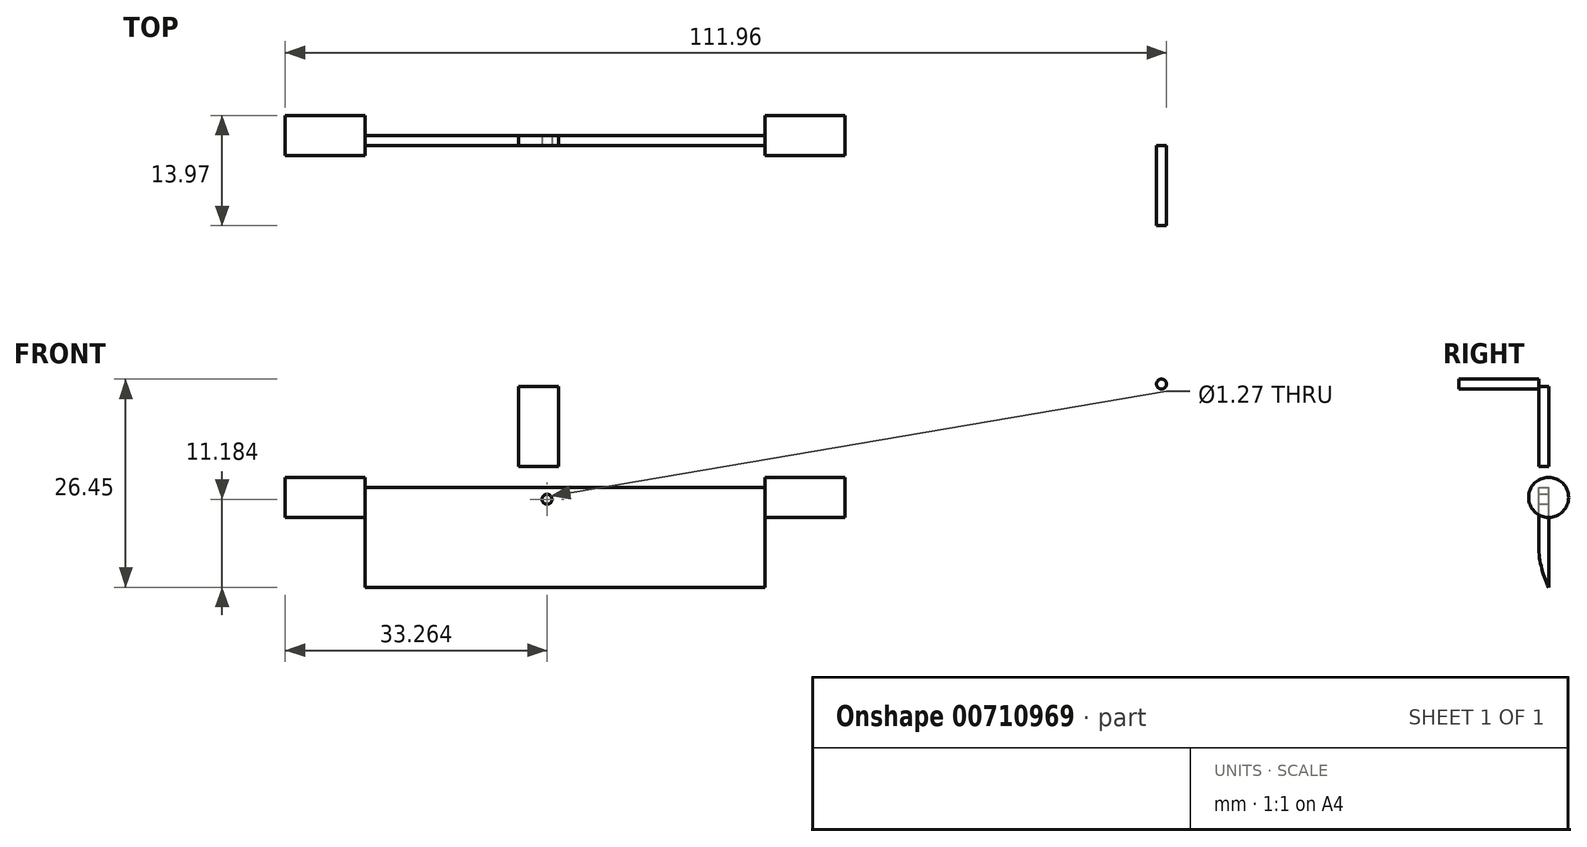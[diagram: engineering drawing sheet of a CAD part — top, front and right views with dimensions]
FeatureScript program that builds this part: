
annotation { "Feature Type Name" : "Feature", "Feature Type Description" : "" }
export const myFeature = defineFeature(function(context is Context, id is Id, definition is map)
    precondition{}
    {
        {
            var Q0;
            Q0=qCreatedBy(makeId("Front.planeOp"),FACE);
            var sketch = newSketch(context, id + "F0", { "sketchPlane" : qUnion([Q0])});
            skLineSegment(sketch, "E0.bottom", {"start": v(2.2, 26.26) * mm, "end": v(-48.6, 26.26) * mm});
            skLineSegment(sketch, "E0.top", {"start": v(2.2, 38.96) * mm, "end": v(-48.6, 38.96) * mm});
            skLineSegment(sketch, "E0.left", {"start": v(2.2, 26.26) * mm, "end": v(2.2, 38.96) * mm});
            skLineSegment(sketch, "E0.right", {"start": v(-48.6, 26.26) * mm, "end": v(-48.6, 38.96) * mm});
            skPoint(sketch, "E0.middle", {"position": v(-23.2, 32.6) * mm});
            skLineSegment(sketch, "E1", {"start": v(-48.6, 37.69) * mm, "end": v(-58.75, 37.69) * mm});
            skLineSegment(sketch, "E2", {"start": v(-58.75, 37.69) * mm, "end": v(-58.75, 35.15) * mm});
            skLineSegment(sketch, "E3", {"start": v(-58.75, 35.15) * mm, "end": v(-48.6, 35.15) * mm});
            skLineSegment(sketch, "E4", {"start": v(2.2, 37.69) * mm, "end": v(12.37, 37.69) * mm});
            skLineSegment(sketch, "E5", {"start": v(12.37, 37.69) * mm, "end": v(12.37, 35.15) * mm});
            skLineSegment(sketch, "E6", {"start": v(12.37, 35.15) * mm, "end": v(2.2, 35.15) * mm});
            skLineSegment(sketch, "E7", {"start": v(-29.08, 45.04) * mm, "end": v(-29.08, 41.6) * mm});
            skLineSegment(sketch, "E8", {"start": v(-29.08, 41.6) * mm, "end": v(-24, 41.6) * mm});
            skLineSegment(sketch, "E9", {"start": v(-24, 41.6) * mm, "end": v(-24, 51.75) * mm});
            skLineSegment(sketch, "E10", {"start": v(-24, 51.75) * mm, "end": v(-29.08, 51.75) * mm});
            skLineSegment(sketch, "E11", {"start": v(-29.08, 51.75) * mm, "end": v(-29.08, 45.04) * mm});
            skSolve(sketch);
        }
        {
            var Q0;
            {var subQ0=sQuery(id+"F0.wireOp",EDGE,"E1");Q0=makeQuery(id+"F0.imprint","IMPRINT",FACE,{"disambiguationData":[TD([[makeQuery(id+"F0.imprint","IMPRINT",EDGE,{"derivedFrom":subQ0}),1.0]])]});}
            var Q1;
            Q1=sQuery(id+"F0.wireOp",EDGE,"E1");
            revolve(context, id + "F1", {"surfaceOperationType" : NewSurfaceOperationType.NEW, "entities" : qUnion([Q0]), "axis" : qUnion([Q1]), "revolveType" : RevolveType.FULL});
        }
        {
            var Q0;
            {var subQ0=sQuery(id+"F0.wireOp",EDGE,"E4");Q0=makeQuery(id+"F0.imprint","IMPRINT",FACE,{"disambiguationData":[TD([[makeQuery(id+"F0.imprint","IMPRINT",EDGE,{"derivedFrom":subQ0}),-1.0]])]});}
            var Q1;
            Q1=sQuery(id+"F0.wireOp",EDGE,"E4");
            revolve(context, id + "F2", {"surfaceOperationType" : NewSurfaceOperationType.NEW, "entities" : qUnion([Q0]), "axis" : qUnion([Q1]), "revolveType" : RevolveType.FULL});
        }
        {
            var Q0;
            {var subQ3=sQuery(id+"F0.wireOp",EDGE,"E0.bottom");Q0=makeQuery(id+"F0.imprint","IMPRINT",FACE,{"disambiguationData":[TD([[makeQuery(id+"F0.imprint","IMPRINT",EDGE,{"derivedFrom":subQ3}),-1.0]])]});}
            extrude(context, id + "F3", {"entities" : qUnion([Q0]), "depth" : 1.27 * mm, "offsetDistance" : 25.4 * mm});
        }
        {
            var Q0;
            Q0=makeQuery(id+"F3.opExtrude","CAP_EDGE",EDGE,{"disambiguationData":[OSD([sQuery(id+"F0.wireOp",EDGE,"E0.bottom")])],"isStart":false});
            fillet(context, id + "F4", {"entities" : qUnion([Q0]), "radius" : 12.7 * mm, "tangentPropagation" : true, "rho" : 0.5, "crossSection" : FilletCrossSection.CONIC, "allowEdgeOverflow" : false});
        }
        {
            var Q0;
            Q0=makeQuery(id+"F3.opExtrude","CAP_FACE",FACE,{"disambiguationData":[OSD([sQuery(id+"F0.wireOp",EDGE,"E0.bottom"),sQuery(id+"F0.wireOp",EDGE,"E0.top"),sQuery(id+"F0.wireOp",EDGE,"E0.left"),sQuery(id+"F0.wireOp",EDGE,"E0.right")])],"isStart":false});
            var sketch = newSketch(context, id + "F5", { "sketchPlane" : qUnion([Q0])});
            skCircle(sketch, "E12", {"center": v(-25.49, 37.44) * mm, "radius": 0.64 * mm});
            skCircle(sketch, "E13", {"center": v(52.57, 52.08) * mm, "radius": 0.64 * mm});
            skSolve(sketch);
        }
        {
            var Q0;
            Q0=makeQuery(id+"F5.imprint","IMPRINT",FACE,{"disambiguationData":[TD([[makeQuery(id+"F5.imprint","IMPRINT",EDGE,{"derivedFrom":sQuery(id+"F5.wireOp",EDGE,"E12")}),1.0]])]});
            extrude(context, id + "F6", {"entities" : qUnion([Q0]), "operationType" : NewBodyOperationType.REMOVE, "endBound" : BoundingType.THROUGH_ALL, "oppositeDirection" : true, "depth" : 25.4 * mm, "offsetDistance" : 25.4 * mm});
        }
        {
            var Q0;
            Q0=makeQuery(id+"F5.imprint","IMPRINT",FACE,{"disambiguationData":[TD([[makeQuery(id+"F5.imprint","IMPRINT",EDGE,{"derivedFrom":sQuery(id+"F5.wireOp",EDGE,"E13")}),1.0]])]});
            extrude(context, id + "F7", {"entities" : qUnion([Q0]), "depth" : 10.16 * mm, "offsetDistance" : 25.4 * mm});
        }
        {
            var Q0;
            Q0=makeQuery(id+"F0.imprint","IMPRINT",FACE,{"disambiguationData":[TD([[makeQuery(id+"F0.imprint","IMPRINT",EDGE,{"derivedFrom":sQuery(id+"F0.wireOp",EDGE,"E7")}),1.0]])]});
            extrude(context, id + "F8", {"entities" : qUnion([Q0]), "depth" : 1.27 * mm, "offsetDistance" : 25.4 * mm});
        }
    });
